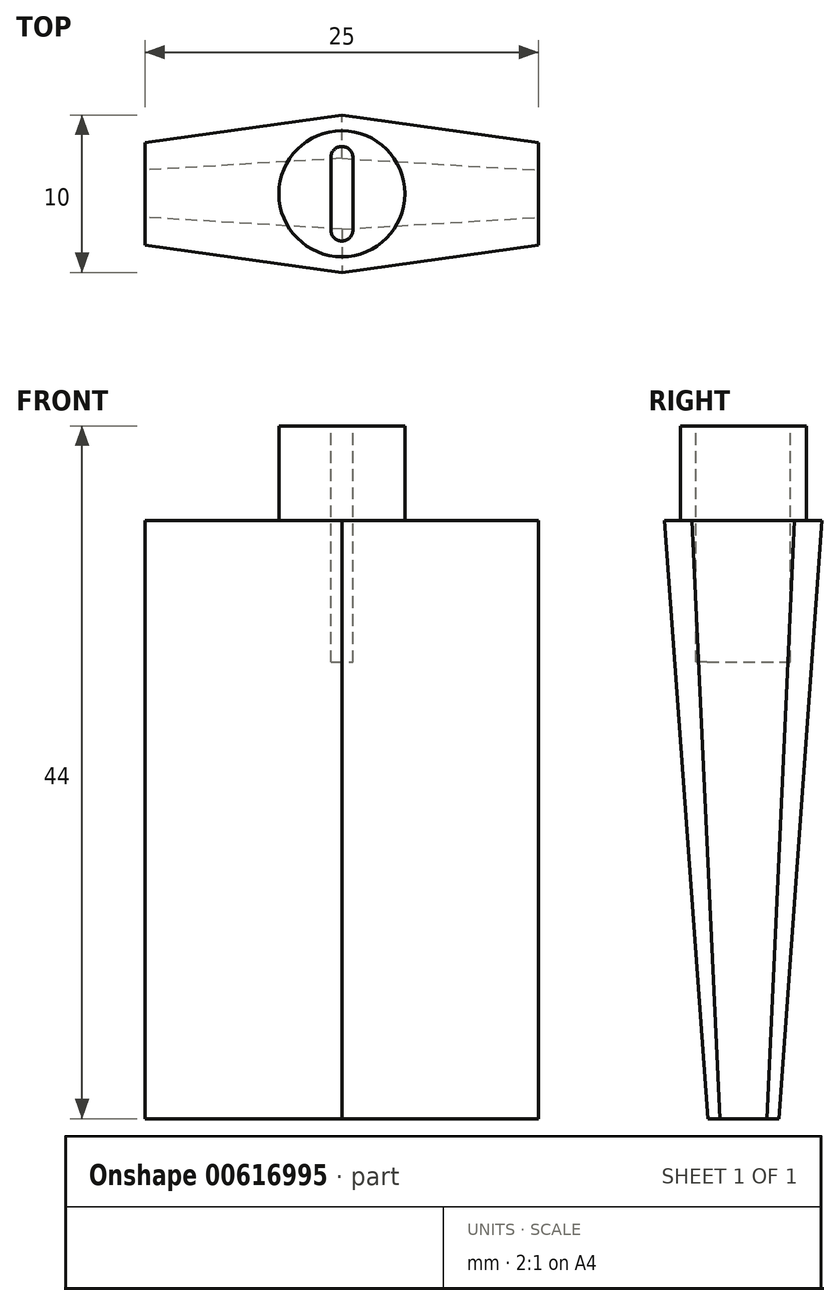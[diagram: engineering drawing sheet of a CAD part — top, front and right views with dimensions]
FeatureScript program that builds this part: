
annotation { "Feature Type Name" : "Feature", "Feature Type Description" : "" }
export const myFeature = defineFeature(function(context is Context, id is Id, definition is map)
    precondition{}
    {
        {
            var Q0;
            Q0=qCreatedBy(makeId("Top.planeOp"),FACE);
            var sketch = newSketch(context, id + "F0", { "sketchPlane" : qUnion([Q0])});
            skLineSegment(sketch, "E0", {"start": v(0, 2.25) * mm, "end": v(-12.5, 1.5) * mm});
            skLineSegment(sketch, "E1", {"start": v(-12.5, 1.5) * mm, "end": v(-12.5, 0) * mm});
            skLineSegment(sketch, "E2.MirrorCS", {"start": v(0, 2.25) * mm, "end": v(12.5, 1.5) * mm});
            skLineSegment(sketch, "E3.MirrorCS", {"start": v(12.5, 1.5) * mm, "end": v(12.5, 0) * mm});
            skLineSegment(sketch, "E4.MirrorCS", {"start": v(-12.5, -1.5) * mm, "end": v(-12.5, 0) * mm});
            skLineSegment(sketch, "E5.MirrorCS", {"start": v(0, -2.25) * mm, "end": v(-12.5, -1.5) * mm});
            skLineSegment(sketch, "E6.MirrorCS", {"start": v(0, -2.25) * mm, "end": v(12.5, -1.5) * mm});
            skLineSegment(sketch, "E7.MirrorCS", {"start": v(12.5, -1.5) * mm, "end": v(12.5, 0) * mm});
            skSolve(sketch);
        }
        {
            var Q0;
            Q0=makeQuery(id+"F0.imprint","IMPRINT",FACE,{"disambiguationData":[TD([[makeQuery(id+"F0.imprint","IMPRINT",EDGE,{"derivedFrom":sQuery(id+"F0.wireOp",EDGE,"E0")}),1.0]])]});
            cPlane(context, id + "F1", {"entities" : qUnion([Q0]), "cplaneType" : CPlaneType.OFFSET, "offset" : 38 * mm, "width" : 150 * mm, "height" : 150 * mm});
        }
        {
            var Q0;
            Q0=qCreatedBy(id+"F1.planeOp",FACE);
            var sketch = newSketch(context, id + "F2", { "sketchPlane" : qUnion([Q0])});
            skLineSegment(sketch, "E8", {"start": v(-51.11, 1.1) * mm, "end": v(-63.61, 0.36) * mm});
            skLineSegment(sketch, "E9", {"start": v(-63.61, 0.36) * mm, "end": v(-63.61, -1.14) * mm});
            skLineSegment(sketch, "E10.MirrorCS", {"start": v(-51.11, 1.1) * mm, "end": v(-38.61, 0.36) * mm});
            skLineSegment(sketch, "E11.MirrorCS", {"start": v(-38.61, 0.36) * mm, "end": v(-38.61, -1.14) * mm});
            skLineSegment(sketch, "E12.MirrorCS", {"start": v(-63.61, -2.64) * mm, "end": v(-63.61, -1.14) * mm});
            skLineSegment(sketch, "E13.MirrorCS", {"start": v(-51.11, -3.4) * mm, "end": v(-63.61, -2.64) * mm});
            skLineSegment(sketch, "E14.MirrorCS", {"start": v(-51.11, -3.4) * mm, "end": v(-38.61, -2.64) * mm});
            skLineSegment(sketch, "E15.MirrorCS", {"start": v(-38.61, -2.64) * mm, "end": v(-38.61, -1.14) * mm});
            skLineSegment(sketch, "E16", {"start": v(-12.5, 0) * mm, "end": v(-12.5, 3.25) * mm});
            skLineSegment(sketch, "E17", {"start": v(-12.5, 3.25) * mm, "end": v(0, 5) * mm});
            skLineSegment(sketch, "E18.MirrorCS", {"start": v(12.5, 3.25) * mm, "end": v(0, 5) * mm});
            skLineSegment(sketch, "E19.MirrorCS", {"start": v(12.5, 0) * mm, "end": v(12.5, 3.25) * mm});
            skLineSegment(sketch, "E20.MirrorCS", {"start": v(-12.5, 0) * mm, "end": v(-12.5, -3.25) * mm});
            skLineSegment(sketch, "E21.MirrorCS", {"start": v(-12.5, -3.25) * mm, "end": v(0, -5) * mm});
            skLineSegment(sketch, "E22.MirrorCS", {"start": v(12.5, -3.25) * mm, "end": v(0, -5) * mm});
            skLineSegment(sketch, "E23.MirrorCS", {"start": v(12.5, 0) * mm, "end": v(12.5, -3.25) * mm});
            skSolve(sketch);
        }
        {
            var Q0;
            Q0=makeQuery(id+"F0.imprint","IMPRINT",FACE,{"disambiguationData":[TD([[makeQuery(id+"F0.imprint","IMPRINT",EDGE,{"derivedFrom":sQuery(id+"F0.wireOp",EDGE,"E0")}),1.0]])]});
            var Q1;
            Q1=makeQuery(id+"F2.imprint","IMPRINT",FACE,{"disambiguationData":[TD([[makeQuery(id+"F2.imprint","IMPRINT",EDGE,{"derivedFrom":sQuery(id+"F2.wireOp",EDGE,"E16")}),-1.0]])]});
            loft(context, id + "F3", {"sheetProfilesArray" : [{ "sheetProfileEntities" : qUnion([Q0]) }, { "sheetProfileEntities" : qUnion([Q1]) }]});
        }
        {
            var Q0;
            Q0=makeQuery(id+"F3.opLoft","CAP_FACE",FACE,{"disambiguationData":[OSD([makeQuery(id+"F2.imprint","IMPRINT",FACE,{"disambiguationData":[TD([[makeQuery(id+"F2.imprint","IMPRINT",EDGE,{"derivedFrom":sQuery(id+"F2.wireOp",EDGE,"E16")}),-1.0]])]})])],"isStart":true});
            var sketch = newSketch(context, id + "F4", { "sketchPlane" : qUnion([Q0])});
            skCircle(sketch, "E24", {"center": v(0, 0) * mm, "radius": 4 * mm});
            skSolve(sketch);
        }
        {
            var Q0;
            Q0=makeQuery(id+"F4.imprint","IMPRINT",FACE,{"disambiguationData":[TD([[makeQuery(id+"F4.imprint","IMPRINT",EDGE,{"derivedFrom":sQuery(id+"F4.wireOp",EDGE,"E24")}),1.0]])]});
            extrude(context, id + "F5", {"entities" : qUnion([Q0]), "operationType" : NewBodyOperationType.ADD, "depth" : 6 * mm, "offsetDistance" : 25 * mm});
        }
        {
            var Q0;
            Q0=makeQuery(id+"F5.opExtrude","CAP_FACE",FACE,{"disambiguationData":[OSD([sQuery(id+"F4.wireOp",EDGE,"E24")])],"isStart":false});
            var sketch = newSketch(context, id + "F6", { "sketchPlane" : qUnion([Q0])});
            skLineSegment(sketch, "E25", {"start": v(-0.7, 0) * mm, "end": v(-0.7, 2.3) * mm});
            skArc(sketch, "E26", {"start": v(0, 3) * mm, "mid": v(-0.5, 2.8) * mm, "end": v(-0.7, 2.3) * mm});
            skArc(sketch, "E27.MirrorCS", {"start": v(0, 3) * mm, "mid": v(0.5, 2.8) * mm, "end": v(0.7, 2.3) * mm});
            skLineSegment(sketch, "E28.MirrorCS", {"start": v(0.7, 0) * mm, "end": v(0.7, 2.3) * mm});
            skLineSegment(sketch, "E29.MirrorCS", {"start": v(0.7, 0) * mm, "end": v(0.7, -2.3) * mm});
            skArc(sketch, "E30.MirrorCS", {"start": v(0, -3) * mm, "mid": v(0.5, -2.8) * mm, "end": v(0.7, -2.3) * mm});
            skArc(sketch, "E31.MirrorCS", {"start": v(0, -3) * mm, "mid": v(-0.5, -2.8) * mm, "end": v(-0.7, -2.3) * mm});
            skLineSegment(sketch, "E32.MirrorCS", {"start": v(-0.7, 0) * mm, "end": v(-0.7, -2.3) * mm});
            skSolve(sketch);
        }
        {
            var Q0;
            Q0=makeQuery(id+"F6.imprint","IMPRINT",FACE,{"disambiguationData":[TD([[makeQuery(id+"F6.imprint","IMPRINT",EDGE,{"derivedFrom":sQuery(id+"F6.wireOp",EDGE,"E25")}),-1.0]])]});
            extrude(context, id + "F7", {"entities" : qUnion([Q0]), "operationType" : NewBodyOperationType.REMOVE, "oppositeDirection" : true, "depth" : 15 * mm, "offsetDistance" : 25 * mm});
        }
    });
